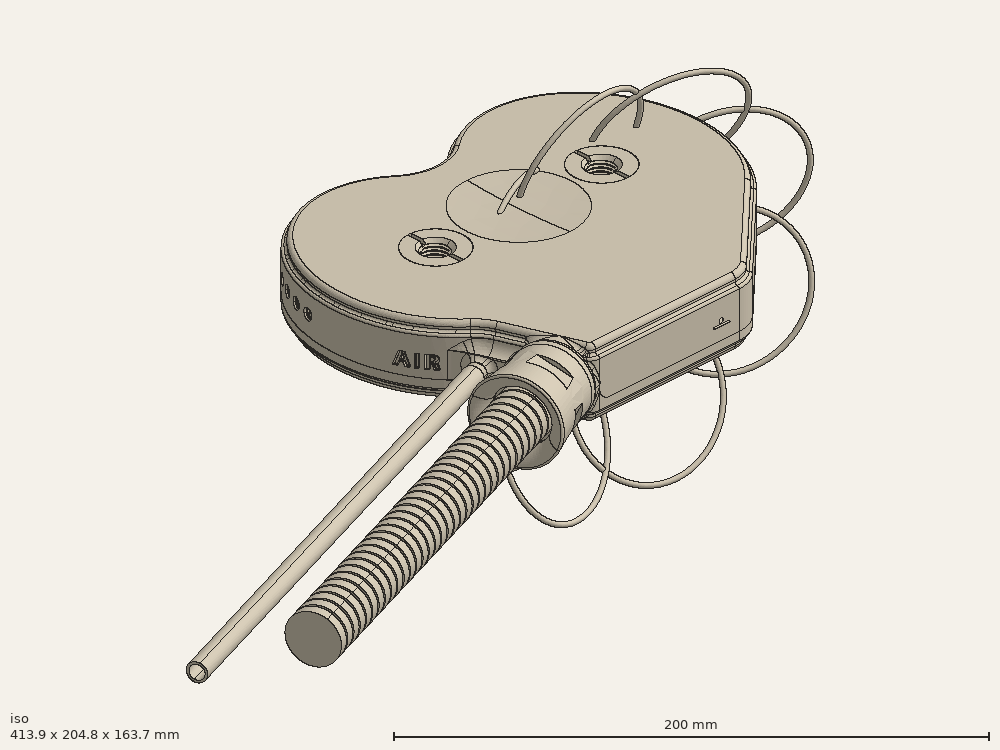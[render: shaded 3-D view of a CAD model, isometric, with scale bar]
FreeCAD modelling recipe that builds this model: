
FCSTD DOCUMENT  (FreeCAD 0.19R24291 (Git))
Label: TMS_8ch_with_loops
License: All rights reserved
LicenseURL: http://en.wikipedia.org/wiki/All_rights_reserved
objects: Sketcher::SketchObject×16, Part::Feature×9, PartDesign::AdditivePipe×8, PartDesign::Body×8, Mesh::Feature×1, Part::FeaturePython×1, App::DocumentObjectGroup×1, App::Part×1
note: 50 computed .brp shape members not serialized (recipe doc carries the construction recipe); baked Part::Feature solids carry a one-line shape summary decoded from their .brp

FEATURE [Mesh::Feature] TMSCompatibleCoilV4_Body
FEATURE [Sketcher::SketchObject] Sketch023
  FullyConstrained = true
  MapMode = 5
  Support = -> [XY_Plane002]
  sketch-geometry (1):
    g0: Circle CenterX=0 CenterY=0 CenterZ=0 NormalX=0 NormalY=0 NormalZ=1 AngleXU=0 Radius=30
  constraints (2):
    c: Coincident(g0,g-1)
    c: Radius(g0) = 30
FEATURE [Sketcher::SketchObject] Sketch001
  FullyConstrained = true
  MapMode = 5
  Placement = pos=(0,0,0) rot=(1,0,0;1.5708rad)
  Support = -> [XZ_Plane002]
  sketch-geometry (1):
    g0: Circle CenterX=30 CenterY=0 CenterZ=0 NormalX=0 NormalY=0 NormalZ=1 AngleXU=0 Radius=1
  constraints (3):
    c: PointOnObject(g0,g-1)
    c: Radius(g0) = 1
    c: DistanceX(g-1,g0) = 30
FEATURE [PartDesign::AdditivePipe] AdditivePipe
  AuxilleryCurvelinear = true
  AuxillerySpineTangent = false
  Binormal = (0,0,0)
  Mode = 0
  Placement = pos=(0,0,0) rot=(1,0,0;1.5708rad)
  Profile = -> Sketch001
  Refine = true
  Spine = -> Sketch023 [Edge1]
  SpineTangent = false
  Transformation = 0
  Transition = 0
FEATURE [PartDesign::Body] Body002  label="loop6cm"
  Group = -> [Sketch023,Sketch001,AdditivePipe]
  Origin = -> Origin002
  Placement = pos=(97.9312,113.135,166.837) rot=(-0.992769,-0.110541,-0.046797;1.23425rad)
  Tip = -> AdditivePipe
FEATURE [Sketcher::SketchObject] Sketch024
  FullyConstrained = true
  MapMode = 5
  Support = -> [XY_Plane003]
  sketch-geometry (1):
    g0: Circle CenterX=0 CenterY=0 CenterZ=0 NormalX=0 NormalY=0 NormalZ=1 AngleXU=0 Radius=30
  constraints (2):
    c: Coincident(g0,g-1)
    c: Radius(g0) = 30
FEATURE [Sketcher::SketchObject] Sketch025
  FullyConstrained = true
  MapMode = 5
  Placement = pos=(0,0,0) rot=(1,0,0;1.5708rad)
  Support = -> [XZ_Plane003]
  sketch-geometry (1):
    g0: Circle CenterX=30 CenterY=0 CenterZ=0 NormalX=0 NormalY=0 NormalZ=1 AngleXU=0 Radius=1
  constraints (3):
    c: PointOnObject(g0,g-1)
    c: Radius(g0) = 1
    c: DistanceX(g-1,g0) = 30
FEATURE [PartDesign::AdditivePipe] AdditivePipe001
  AuxilleryCurvelinear = true
  AuxillerySpineTangent = false
  Binormal = (0,0,0)
  Mode = 0
  Placement = pos=(0,0,0) rot=(1,0,0;1.5708rad)
  Profile = -> Sketch025
  Refine = true
  Spine = -> Sketch024 [Edge1]
  SpineTangent = false
  Transformation = 0
  Transition = 0
FEATURE [PartDesign::Body] Body003  label="loop6cm001"
  Group = -> [Sketch024,Sketch025,AdditivePipe001]
  Origin = -> Origin003
  Placement = pos=(139.6,112.193,162.584) rot=(-0.88393,0.41877,0.208084;1.16451rad)
  Tip = -> AdditivePipe001
FEATURE [Sketcher::SketchObject] Sketch026
  FullyConstrained = true
  MapMode = 5
  Support = -> [XY_Plane004]
  sketch-geometry (1):
    g0: Circle CenterX=0 CenterY=0 CenterZ=0 NormalX=0 NormalY=0 NormalZ=1 AngleXU=0 Radius=30
  constraints (2):
    c: Coincident(g0,g-1)
    c: Radius(g0) = 30
FEATURE [Sketcher::SketchObject] Sketch027
  FullyConstrained = true
  MapMode = 5
  Placement = pos=(0,0,0) rot=(1,0,0;1.5708rad)
  Support = -> [XZ_Plane004]
  sketch-geometry (1):
    g0: Circle CenterX=30 CenterY=0 CenterZ=0 NormalX=0 NormalY=0 NormalZ=1 AngleXU=0 Radius=1
  constraints (3):
    c: PointOnObject(g0,g-1)
    c: Radius(g0) = 1
    c: DistanceX(g-1,g0) = 30
FEATURE [PartDesign::AdditivePipe] AdditivePipe002
  AuxilleryCurvelinear = true
  AuxillerySpineTangent = false
  Binormal = (0,0,0)
  Mode = 0
  Placement = pos=(0,0,0) rot=(1,0,0;1.5708rad)
  Profile = -> Sketch027
  Refine = true
  Spine = -> Sketch026 [Edge1]
  SpineTangent = false
  Transformation = 0
  Transition = 0
FEATURE [PartDesign::Body] Body004  label="loop6cm002"
  Group = -> [Sketch026,Sketch027,AdditivePipe002]
  Origin = -> Origin004
  Placement = pos=(166.334,111.703,132.682) rot=(-0.556428,0.700676,0.446587;1.57194rad)
  Tip = -> AdditivePipe002
FEATURE [Sketcher::SketchObject] Sketch028
  FullyConstrained = true
  MapMode = 5
  Support = -> [XY_Plane005]
  sketch-geometry (1):
    g0: Circle CenterX=0 CenterY=0 CenterZ=0 NormalX=0 NormalY=0 NormalZ=1 AngleXU=0 Radius=30
  constraints (2):
    c: Coincident(g0,g-1)
    c: Radius(g0) = 30
FEATURE [Sketcher::SketchObject] Sketch029
  FullyConstrained = true
  MapMode = 5
  Placement = pos=(0,0,0) rot=(1,0,0;1.5708rad)
  Support = -> [XZ_Plane005]
  sketch-geometry (1):
    g0: Circle CenterX=30 CenterY=0 CenterZ=0 NormalX=0 NormalY=0 NormalZ=1 AngleXU=0 Radius=1
  constraints (3):
    c: PointOnObject(g0,g-1)
    c: Radius(g0) = 1
    c: DistanceX(g-1,g0) = 30
FEATURE [PartDesign::AdditivePipe] AdditivePipe003
  AuxilleryCurvelinear = true
  AuxillerySpineTangent = false
  Binormal = (0,0,0)
  Mode = 0
  Placement = pos=(0,0,0) rot=(1,0,0;1.5708rad)
  Profile = -> Sketch029
  Refine = true
  Spine = -> Sketch028 [Edge1]
  SpineTangent = false
  Transformation = 0
  Transition = 0
FEATURE [PartDesign::Body] Body005  label="loop6cm003"
  Group = -> [Sketch028,Sketch029,AdditivePipe003]
  Origin = -> Origin005
  Placement = pos=(166.75,111.628,88.708) rot=(-0.822642,0.561797,0.087429;1.7425rad)
  Tip = -> AdditivePipe003
FEATURE [Sketcher::SketchObject] Sketch030
  FullyConstrained = true
  MapMode = 5
  Support = -> [XY_Plane006]
  sketch-geometry (1):
    g0: Circle CenterX=0 CenterY=0 CenterZ=0 NormalX=0 NormalY=0 NormalZ=1 AngleXU=0 Radius=30
  constraints (2):
    c: Coincident(g0,g-1)
    c: Radius(g0) = 30
FEATURE [Sketcher::SketchObject] Sketch031
  FullyConstrained = true
  MapMode = 5
  Placement = pos=(0,0,0) rot=(1,0,0;1.5708rad)
  Support = -> [XZ_Plane006]
  sketch-geometry (1):
    g0: Circle CenterX=30 CenterY=0 CenterZ=0 NormalX=0 NormalY=0 NormalZ=1 AngleXU=0 Radius=1
  constraints (3):
    c: PointOnObject(g0,g-1)
    c: Radius(g0) = 1
    c: DistanceX(g-1,g0) = 30
FEATURE [PartDesign::AdditivePipe] AdditivePipe004
  AuxilleryCurvelinear = true
  AuxillerySpineTangent = false
  Binormal = (0,0,0)
  Mode = 0
  Placement = pos=(0,0,0) rot=(1,0,0;1.5708rad)
  Profile = -> Sketch031
  Refine = true
  Spine = -> Sketch030 [Edge1]
  SpineTangent = false
  Transformation = 0
  Transition = 0
FEATURE [PartDesign::Body] Body006  label="loop6cm004"
  Group = -> [Sketch030,Sketch031,AdditivePipe004]
  Origin = -> Origin006
  Placement = pos=(131.808,114.583,60.4981) rot=(-0.076426,0.852091,0.517784;2.85076rad)
  Tip = -> AdditivePipe004
FEATURE [Sketcher::SketchObject] Sketch032
  FullyConstrained = true
  MapMode = 5
  Support = -> [XY_Plane007]
  sketch-geometry (1):
    g0: Circle CenterX=0 CenterY=0 CenterZ=0 NormalX=0 NormalY=0 NormalZ=1 AngleXU=0 Radius=30
  constraints (2):
    c: Coincident(g0,g-1)
    c: Radius(g0) = 30
FEATURE [Sketcher::SketchObject] Sketch033
  FullyConstrained = true
  MapMode = 5
  Placement = pos=(0,0,0) rot=(1,0,0;1.5708rad)
  Support = -> [XZ_Plane007]
  sketch-geometry (1):
    g0: Circle CenterX=30 CenterY=0 CenterZ=0 NormalX=0 NormalY=0 NormalZ=1 AngleXU=0 Radius=1
  constraints (3):
    c: PointOnObject(g0,g-1)
    c: Radius(g0) = 1
    c: DistanceX(g-1,g0) = 30
FEATURE [PartDesign::AdditivePipe] AdditivePipe005
  AuxilleryCurvelinear = true
  AuxillerySpineTangent = false
  Binormal = (0,0,0)
  Mode = 0
  Placement = pos=(0,0,0) rot=(1,0,0;1.5708rad)
  Profile = -> Sketch033
  Refine = true
  Spine = -> Sketch032 [Edge1]
  SpineTangent = false
  Transformation = 0
  Transition = 0
FEATURE [PartDesign::Body] Body007  label="loop6cm005"
  Group = -> [Sketch032,Sketch033,AdditivePipe005]
  Origin = -> Origin007
  Placement = pos=(86.716,113.83,63.7104) rot=(0.136429,0.848281,0.51167;3.59473rad)
  Tip = -> AdditivePipe005
FEATURE [Sketcher::SketchObject] Sketch034
  FullyConstrained = true
  MapMode = 5
  Placement = pos=(0,0,0) rot=(1,0,0;1.5708rad)
  Support = -> [XZ_Plane008]
  sketch-geometry (1):
    g0: Circle CenterX=30 CenterY=0 CenterZ=0 NormalX=0 NormalY=0 NormalZ=1 AngleXU=0 Radius=1
  constraints (3):
    c: PointOnObject(g0,g-1)
    c: Radius(g0) = 1
    c: DistanceX(g-1,g0) = 30
FEATURE [Sketcher::SketchObject] Sketch035
  FullyConstrained = true
  MapMode = 5
  Support = -> [XY_Plane008]
  sketch-geometry (1):
    g0: Circle CenterX=0 CenterY=0 CenterZ=0 NormalX=0 NormalY=0 NormalZ=1 AngleXU=0 Radius=30
  constraints (2):
    c: Coincident(g0,g-1)
    c: Radius(g0) = 30
FEATURE [PartDesign::AdditivePipe] AdditivePipe006
  AuxilleryCurvelinear = true
  AuxillerySpineTangent = false
  Binormal = (0,0,0)
  Mode = 0
  Placement = pos=(0,0,0) rot=(1,0,0;1.5708rad)
  Profile = -> Sketch034
  Refine = true
  Spine = -> Sketch035 [Edge1]
  SpineTangent = false
  Transformation = 0
  Transition = 0
FEATURE [PartDesign::Body] Body008  label="loop6cm006"
  Group = -> [Sketch035,Sketch034,AdditivePipe006]
  Origin = -> Origin008
  Placement = pos=(62.2454,112.129,96.4052) rot=(0.388464,0.817882,0.424458;4.17586rad)
  Tip = -> AdditivePipe006
FEATURE [Sketcher::SketchObject] Sketch036
  FullyConstrained = true
  MapMode = 5
  Placement = pos=(0,0,0) rot=(1,0,0;1.5708rad)
  Support = -> [XZ_Plane009]
  sketch-geometry (1):
    g0: Circle CenterX=30 CenterY=0 CenterZ=0 NormalX=0 NormalY=0 NormalZ=1 AngleXU=0 Radius=1
  constraints (3):
    c: PointOnObject(g0,g-1)
    c: Radius(g0) = 1
    c: DistanceX(g-1,g0) = 30
FEATURE [Sketcher::SketchObject] Sketch037
  FullyConstrained = true
  MapMode = 5
  Support = -> [XY_Plane009]
  sketch-geometry (1):
    g0: Circle CenterX=0 CenterY=0 CenterZ=0 NormalX=0 NormalY=0 NormalZ=1 AngleXU=0 Radius=30
  constraints (2):
    c: Coincident(g0,g-1)
    c: Radius(g0) = 30
FEATURE [PartDesign::AdditivePipe] AdditivePipe007
  AuxilleryCurvelinear = true
  AuxillerySpineTangent = false
  Binormal = (0,0,0)
  Mode = 0
  Placement = pos=(0,0,0) rot=(1,0,0;1.5708rad)
  Profile = -> Sketch036
  Refine = true
  Spine = -> Sketch037 [Edge1]
  SpineTangent = false
  Transformation = 0
  Transition = 0
FEATURE [PartDesign::Body] Body009  label="loop6cm007"
  Group = -> [Sketch037,Sketch036,AdditivePipe007]
  Origin = -> Origin009
  Placement = pos=(69.3575,115.9,140.009) rot=(-0.664687,-0.6319,-0.398615;1.64689rad)
  Tip = -> AdditivePipe007
FEATURE [Part::FeaturePython] Clone  label="_1091_FemaleHead_v4004"  # WARN: FeaturePython — macro-defined, semantics opaque (R4)
  AttacherType = Attacher::AttachEngine3D
  Fuse = false
  Placement = pos=(-46.5854,-86.4835,126.222) rot=(0.785809,-0.17421,0.593426;4.13769rad)
  Scale = (1.5,1.5,1.5)
FEATURE [App::DocumentObjectGroup] Group  label="8ch"
  Group = -> [TMSCompatibleCoilV4_Body,Body002,Body003,Body004,Body005,Body006,Body007,Body008,Body009]
FEATURE [Part::Feature] Part__Feature  label="HC-T643-v3 MRi B91 Air grade Underpart"
  Placement = pos=(61.9468,105.579,136.707) rot=(0,0,1;0rad)
  shape: bbox 225 x 143.2 x 27.01 mm, 683 faces (baked)
FEATURE [Part::Feature] Part__Feature001  label="hc-t623-v1.3 MRi b91 aflaster halvpart L"
  Placement = pos=(22.5969,30.3851,156.107) rot=(-0.045589,0.25855,0.964922;3.47865rad)
  shape: bbox 37.54 x 32.61 x 24.84 mm, 155 faces (baked)
FEATURE [Part::Feature] Part__Feature002  label="hc-t624-v1.3 MRi b91 aflaster halvpart R"
  Placement = pos=(16.4442,44.3659,147.307) rot=(-0.167901,0.952213,-0.255145;3.05167rad)
  shape: bbox 37.73 x 32.82 x 24.88 mm, 149 faces (baked)
FEATURE [Part::Feature] Part__Feature003  label="hc-t626-v1 MRi b91 aflaster omløber"
  Placement = pos=(9.41861,28.3611,163.266) rot=(-0.096284,0.546053,0.832199;3.43299rad)
  shape: bbox 160.1 x 135.9 x 144.6 mm, 75 faces (baked)
FEATURE [Part::Feature] Part__Feature004  label="HC-T645-v3 MRi B91 Air grade Overpart"
  Placement = pos=(61.9468,105.579,157.207) rot=(0,0,1;0rad)
  shape: bbox 225.1 x 143.7 x 37.19 mm, 715 faces (baked)
FEATURE [Part::Feature] Part__Feature005  label="ֲ1 Astroflex"
  Placement = pos=(-172.735,-32.5997,151.707) rot=(-0.640255,-0.303782,0.705542;3.00882rad)
  shape: bbox 166.5 x 77.53 x 21 mm, 205 faces (baked)
FEATURE [Part::Feature] Part__Feature006  label="Slange ֶָ"
  Placement = pos=(-11.5384,53.7396,151.707) rot=(-0.671277,-0.222695,0.706961;3.18224rad)
  shape: bbox 209.5 x 82.76 x 8 mm, 6 faces (baked)
FEATURE [Part::Feature] Part__Feature007  label="hc-t432-v3 Center anker"
  Placement = pos=(101.447,105.579,137.707) rot=(0,0,1;0rad)
  shape: bbox 25 x 25 x 29.6 mm, 100 faces (baked)
FEATURE [Part::Feature] Part__Feature008  label="hc-t432-v3 Center anker001"
  Placement = pos=(22.4468,105.579,137.707) rot=(0,0,1;0rad)
  shape: bbox 25 x 25 x 29.6 mm, 100 faces (baked)
FEATURE [App::Part] MRI_B91_External_Parts  label="MRI B91 External Parts"
  Group = -> [Part__Feature,Part__Feature001,Part__Feature002,Part__Feature003,Part__Feature004,Part__Feature005,Part__Feature006,Part__Feature007,Part__Feature008]
  Origin = -> Origin
  Placement = pos=(56,-25,218) rot=(1,0,0;4.71239rad)
